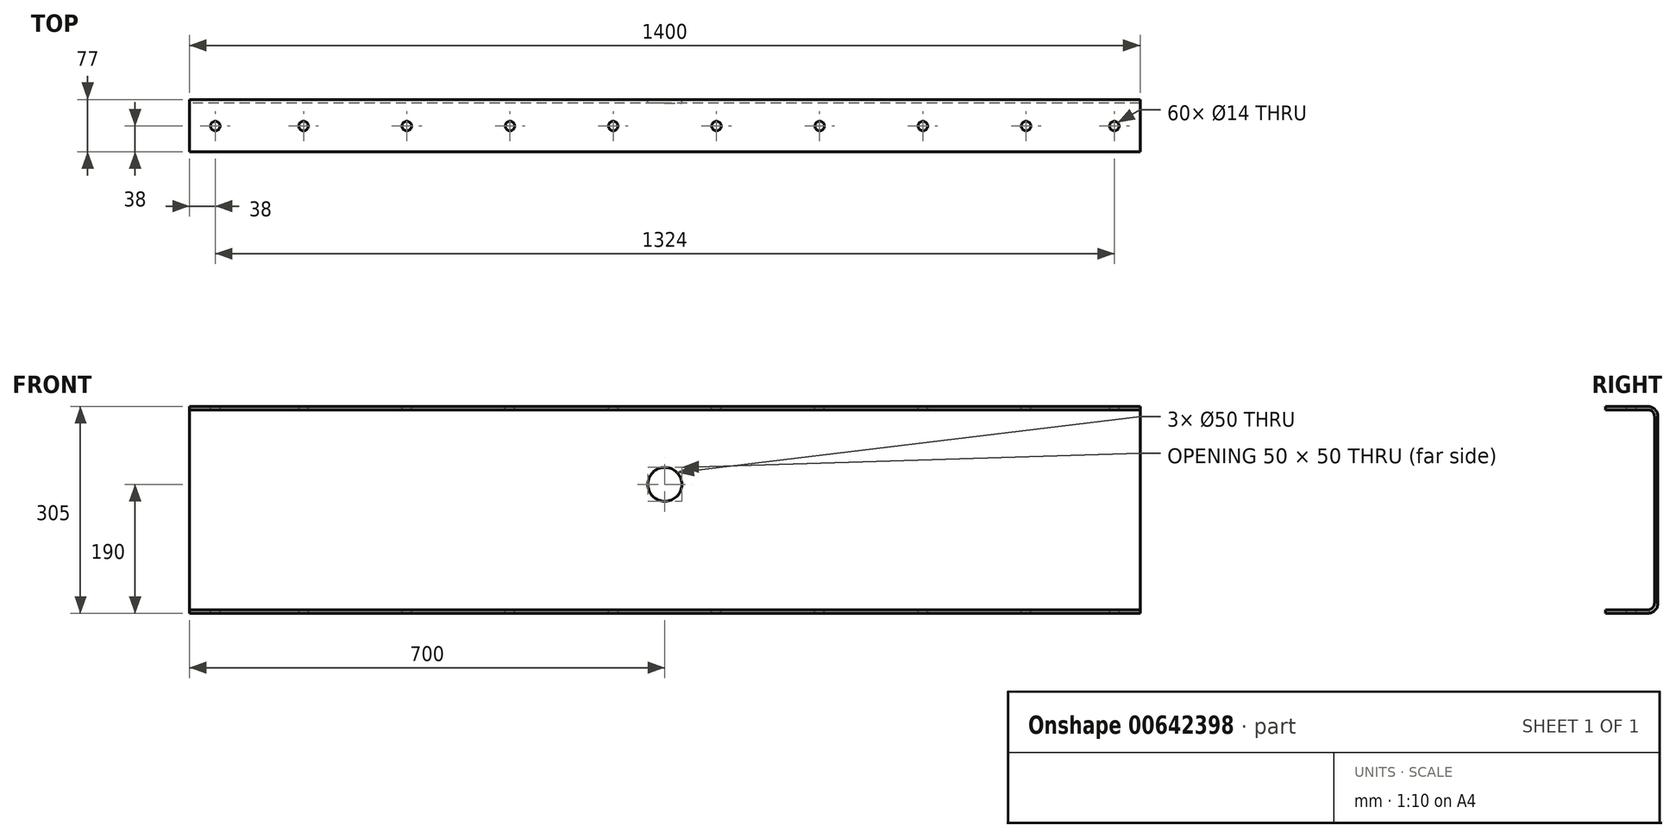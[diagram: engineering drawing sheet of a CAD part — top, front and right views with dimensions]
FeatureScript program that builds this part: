
annotation { "Feature Type Name" : "Feature", "Feature Type Description" : "" }
export const myFeature = defineFeature(function(context is Context, id is Id, definition is map)
    precondition{}
    {
        {
            var Q0;
            Q0=qCreatedBy(makeId("Right.planeOp"),FACE);
            var sketch = newSketch(context, id + "F0", { "sketchPlane" : qUnion([Q0])});
            skLineSegment(sketch, "E0.bottom", {"start": v(0, 0) * mm, "end": v(62, 0) * mm});
            skLineSegment(sketch, "E0.top", {"start": v(0, 305) * mm, "end": v(62, 305) * mm});
            skLineSegment(sketch, "E0.left", {"start": v(0, 0) * mm, "end": v(0, 5) * mm});
            skLineSegment(sketch, "E0.right", {"start": v(77, 15) * mm, "end": v(77, 290) * mm});
            skLineSegment(sketch, "E1.0", {"start": v(0, 5) * mm, "end": v(62, 5) * mm});
            skLineSegment(sketch, "E1.1", {"start": v(72, 15) * mm, "end": v(72, 290) * mm});
            skLineSegment(sketch, "E1.2", {"start": v(0, 300) * mm, "end": v(62, 300) * mm});
            skLineSegment(sketch, "E2.trimOffspring", {"start": v(0, 300) * mm, "end": v(0, 305) * mm});
            skPoint(sketch, "E3.visualSharp", {"position": v(72, 300) * mm});
            skArc(sketch, "E3.filletArc", {"start": v(72, 290) * mm, "mid": v(69.07, 297.07) * mm, "end": v(62, 300) * mm});
            skPoint(sketch, "E4.visualSharp", {"position": v(72, 5) * mm});
            skArc(sketch, "E4.filletArc", {"start": v(62, 5) * mm, "mid": v(69.07, 7.93) * mm, "end": v(72, 15) * mm});
            skPoint(sketch, "E5.visualSharp", {"position": v(77, 0) * mm});
            skArc(sketch, "E5.filletArc", {"start": v(62, 0) * mm, "mid": v(72.6, 4.4) * mm, "end": v(77, 15) * mm});
            skPoint(sketch, "E6.visualSharp", {"position": v(77, 305) * mm});
            skArc(sketch, "E6.filletArc", {"start": v(77, 290) * mm, "mid": v(72.6, 300.6) * mm, "end": v(62, 305) * mm});
            skSolve(sketch);
        }
        {
            var Q0;
            Q0=makeQuery(id+"F0.imprint","IMPRINT",FACE,{"disambiguationData":[TD([[makeQuery(id+"F0.imprint","IMPRINT",EDGE,{"derivedFrom":sQuery(id+"F0.wireOp",EDGE,"E0.bottom")}),1.0]])]});
            extrude(context, id + "F1", {"entities" : qUnion([Q0]), "depth" : 1400 * mm, "offsetDistance" : 25 * mm});
        }
        {
            var Q0;
            Q0=makeQuery(id+"F1.opExtrude","SWEPT_FACE",FACE,{"disambiguationData":[OSD([sQuery(id+"F0.wireOp",EDGE,"E0.right")])]});
            var sketch = newSketch(context, id + "F2", { "sketchPlane" : qUnion([Q0])});
            skLineSegment(sketch, "E7.0", {"start": v(-1400, 0) * mm, "end": v(0, 0) * mm});
            skLineSegment(sketch, "E8", {"start": v(-700, 0) * mm, "end": v(-700, 190) * mm, "construction": true});
            skCircle(sketch, "E9", {"center": v(-700, 190) * mm, "radius": 25 * mm});
            skSolve(sketch);
        }
        {
            var Q0;
            Q0=makeQuery(id+"F2.imprint","IMPRINT",FACE,{"disambiguationData":[TD([[makeQuery(id+"F2.imprint","IMPRINT",EDGE,{"derivedFrom":sQuery(id+"F2.wireOp",EDGE,"E9")}),1.0]])]});
            extrude(context, id + "F3", {"entities" : qUnion([Q0]), "operationType" : NewBodyOperationType.REMOVE, "endBound" : BoundingType.UP_TO_NEXT, "oppositeDirection" : true, "depth" : 25 * mm, "offsetDistance" : 25 * mm});
        }
        {
            var Q0;
            Q0=makeQuery(id+"F1.opExtrude","SWEPT_FACE",FACE,{"disambiguationData":[OSD([sQuery(id+"F0.wireOp",EDGE,"E0.top")])]});
            var sketch = newSketch(context, id + "F4", { "sketchPlane" : qUnion([Q0])});
            skLineSegment(sketch, "E10", {"start": v(700, 0) * mm, "end": v(700, 38) * mm});
            skLineSegment(sketch, "E11.0", {"start": v(776, 0) * mm, "end": v(776, 38) * mm});
            skCircle(sketch, "E12", {"center": v(776, 38) * mm, "radius": 7 * mm});
            skCircle(sketch, "E13.1.0.0", {"center": v(928, 38) * mm, "radius": 7 * mm});
            skCircle(sketch, "E13.2.0.0", {"center": v(1080, 38) * mm, "radius": 7 * mm});
            skCircle(sketch, "E13.3.0.0", {"center": v(1232, 38) * mm, "radius": 7 * mm});
            skLineSegment(sketch, "E13.direction1", {"start": v(776, 38) * mm, "end": v(928, 38) * mm, "construction": true});
            skCircle(sketch, "E14", {"center": v(1362, 38) * mm, "radius": 7 * mm});
            skCircle(sketch, "E15.MirrorC", {"center": v(624, 38) * mm, "radius": 7 * mm});
            skCircle(sketch, "E16.MirrorC", {"center": v(472, 38) * mm, "radius": 7 * mm});
            skCircle(sketch, "E17.MirrorC", {"center": v(320, 38) * mm, "radius": 7 * mm});
            skCircle(sketch, "E18.MirrorC", {"center": v(168, 38) * mm, "radius": 7 * mm});
            skCircle(sketch, "E19.MirrorC", {"center": v(38, 38) * mm, "radius": 7 * mm});
            skSolve(sketch);
        }
        {
            var Q0;
            Q0=makeQuery(id+"F4.imprint","IMPRINT",FACE,{"disambiguationData":[TD([[makeQuery(id+"F4.imprint","IMPRINT",EDGE,{"derivedFrom":sQuery(id+"F4.wireOp",EDGE,"E12")}),1.0]])]});
            var Q1;
            Q1=makeQuery(id+"F4.imprint","IMPRINT",FACE,{"disambiguationData":[TD([[makeQuery(id+"F4.imprint","IMPRINT",EDGE,{"derivedFrom":sQuery(id+"F4.wireOp",EDGE,"E13.1.0.0")}),1.0]])]});
            var Q2;
            Q2=makeQuery(id+"F4.imprint","IMPRINT",FACE,{"disambiguationData":[TD([[makeQuery(id+"F4.imprint","IMPRINT",EDGE,{"derivedFrom":sQuery(id+"F4.wireOp",EDGE,"E13.2.0.0")}),1.0]])]});
            var Q3;
            Q3=makeQuery(id+"F4.imprint","IMPRINT",FACE,{"disambiguationData":[TD([[makeQuery(id+"F4.imprint","IMPRINT",EDGE,{"derivedFrom":sQuery(id+"F4.wireOp",EDGE,"E13.3.0.0")}),1.0]])]});
            var Q4;
            Q4=makeQuery(id+"F4.imprint","IMPRINT",FACE,{"disambiguationData":[TD([[makeQuery(id+"F4.imprint","IMPRINT",EDGE,{"derivedFrom":sQuery(id+"F4.wireOp",EDGE,"E14")}),1.0]])]});
            extrude(context, id + "F5", {"entities" : qUnion([Q0, Q1, Q2, Q3, Q4]), "operationType" : NewBodyOperationType.REMOVE, "endBound" : BoundingType.THROUGH_ALL, "oppositeDirection" : true, "depth" : 25 * mm, "offsetDistance" : 25 * mm});
        }
        {
            var Q0;
            Q0 = qSketchRegion(id + "F4", true);
            extrude(context, id + "F6", {"entities" : qUnion([Q0]), "operationType" : NewBodyOperationType.REMOVE, "endBound" : BoundingType.THROUGH_ALL, "oppositeDirection" : true, "depth" : 25 * mm, "offsetDistance" : 25 * mm});
        }
    });
